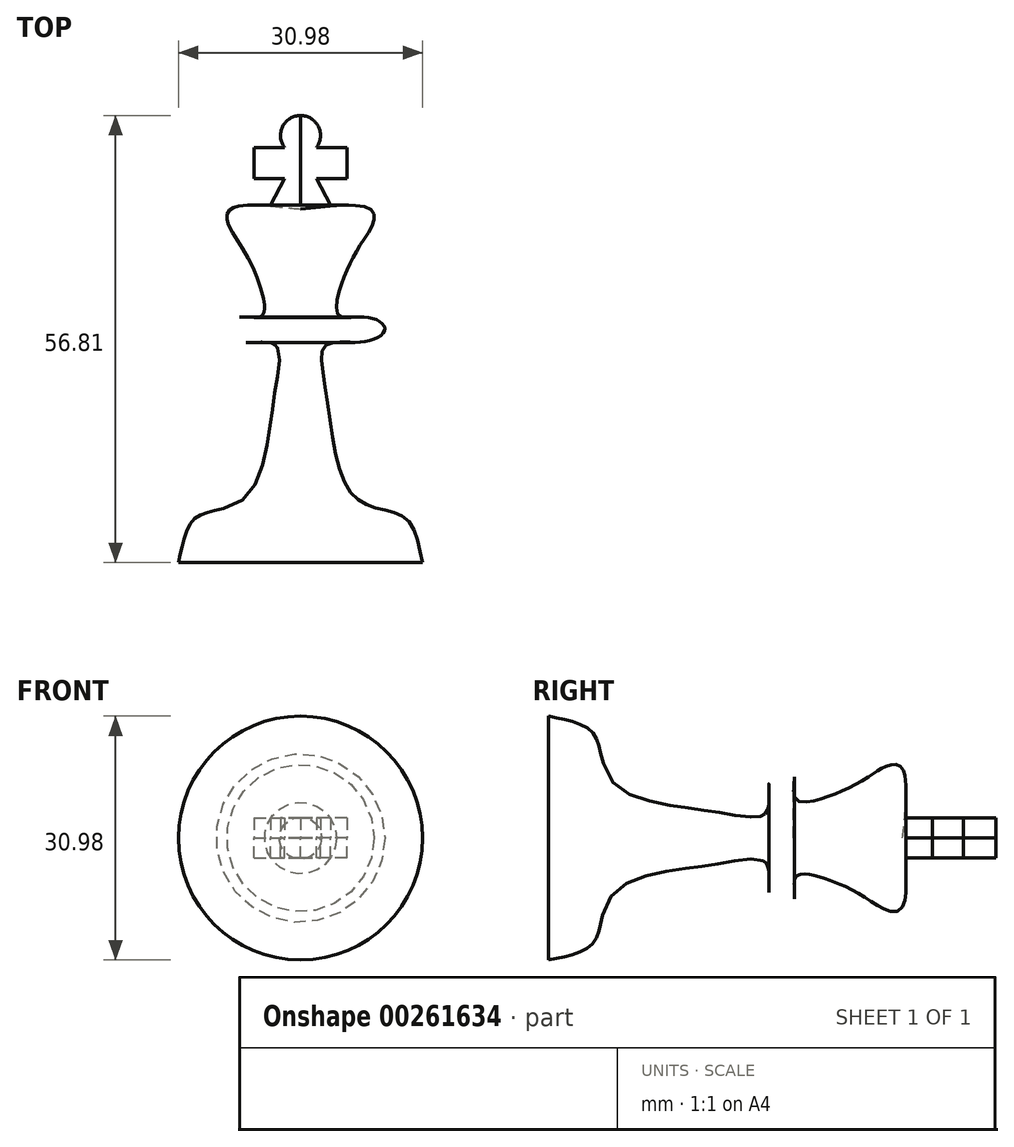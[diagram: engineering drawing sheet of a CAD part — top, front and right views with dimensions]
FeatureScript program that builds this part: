
annotation { "Feature Type Name" : "Feature", "Feature Type Description" : "" }
export const myFeature = defineFeature(function(context is Context, id is Id, definition is map)
    precondition{}
    {
        {
            var Q0;
            Q0=qCreatedBy(makeId("Top.planeOp"),FACE);
            var sketch = newSketch(context, id + "F0", { "sketchPlane" : qUnion([Q0])});
            skLineSegment(sketch, "E0", {"start": v(0, 0) * mm, "end": v(15.5, 0) * mm});
            skLineSegment(sketch, "E1", {"start": v(0, 0) * mm, "end": v(0, 44.92) * mm});
            skFitSpline(sketch, "E2", {"points": [v(0, 44.92) * mm, v(8.84, 44.92) * mm, v(9.25, 43.26) * mm, v(7.6, 40.35) * mm, v(6.14, 37.64) * mm, v(4.89, 34.32) * mm, v(4.89, 31.4) * mm, v(8.42, 31.2) * mm, v(10.71, 29.74) * mm, v(8.21, 28.08) * mm, v(3.22, 27.66) * mm, v(3.22, 21.84) * mm, v(5.93, 9.57) * mm, v(9.88, 6.86) * mm, v(13.62, 5.4) * mm, v(15.5, 0) * mm], "startDerivative": vector(118.77, 13.18) * mm, "endDerivative": vector(15.68, -75.67) * mm});
            skSolve(sketch);
        }
        {
            var Q0;
            Q0=makeQuery(id+"F0.imprint","IMPRINT",FACE,{"disambiguationData":[TD([[makeQuery(id+"F0.imprint","IMPRINT",EDGE,{"derivedFrom":sQuery(id+"F0.wireOp",EDGE,"E0")}),1.0]])]});
            var Q1;
            Q1=sQuery(id+"F0.wireOp",EDGE,"E1");
            revolve(context, id + "F1", {"entities" : qUnion([Q0]), "axis" : qUnion([Q1]), "revolveType" : RevolveType.FULL});
        }
        {
            var Q0;
            Q0=qCreatedBy(makeId("Top.planeOp"),FACE);
            var sketch = newSketch(context, id + "F2", { "sketchPlane" : qUnion([Q0])});
            skLineSegment(sketch, "E3", {"start": v(-3.81, 45.43) * mm, "end": v(-2.02, 48.8) * mm});
            skLineSegment(sketch, "E4", {"start": v(-2.02, 48.8) * mm, "end": v(-5.9, 48.8) * mm});
            skLineSegment(sketch, "E5", {"start": v(-5.9, 48.8) * mm, "end": v(-5.9, 52.73) * mm});
            skLineSegment(sketch, "E6", {"start": v(-5.9, 52.73) * mm, "end": v(-2.02, 52.73) * mm});
            skArc(sketch, "E7", {"start": v(0, 56.81) * mm, "mid": v(-2.28, 55.4) * mm, "end": v(-2.02, 52.73) * mm});
            skLineSegment(sketch, "E8", {"start": v(-3.8, 45.43) * mm, "end": v(0, 45.43) * mm});
            skLineSegment(sketch, "E9", {"start": v(0, 56.81) * mm, "end": v(0, 45.43) * mm});
            skSolve(sketch);
        }
        {
            var Q0;
            Q0 = qSketchRegion(id + "F2", true);
            extrude(context, id + "F3", {"entities" : qUnion([Q0]), "operationType" : NewBodyOperationType.ADD, "depth" : 2.54 * mm});
        }
        {
            var Q0;
            Q0=makeQuery(id+"F3.opExtrude","SWEPT_BODY",BODY,{"disambiguationData":[OSD([sQuery(id+"F2.wireOp",EDGE,"E3"),sQuery(id+"F2.wireOp",EDGE,"E4"),sQuery(id+"F2.wireOp",EDGE,"E5"),sQuery(id+"F2.wireOp",EDGE,"E6"),sQuery(id+"F2.wireOp",EDGE,"E7"),sQuery(id+"F2.wireOp",EDGE,"E8"),sQuery(id+"F2.wireOp",EDGE,"E9")])]});
            var Q1;
            Q1=qCreatedBy(makeId("Right.planeOp"),FACE);
            mirror(context, id + "F4", {"operationType" : NewBodyOperationType.ADD, "entities" : qUnion([Q0]), "mirrorPlane" : qUnion([Q1])});
        }
        {
            var Q0;
            Q0=makeQuery(id+"F4.opPattern","COPY",BODY,{"derivedFrom":makeQuery(id+"F3.opExtrude","SWEPT_BODY",BODY,{"disambiguationData":[OSD([sQuery(id+"F2.wireOp",EDGE,"E3"),sQuery(id+"F2.wireOp",EDGE,"E4"),sQuery(id+"F2.wireOp",EDGE,"E5"),sQuery(id+"F2.wireOp",EDGE,"E6"),sQuery(id+"F2.wireOp",EDGE,"E7"),sQuery(id+"F2.wireOp",EDGE,"E8"),sQuery(id+"F2.wireOp",EDGE,"E9")])]}),"instanceName":"1"});
            var Q1;
            Q1=makeQuery(id+"F3.opExtrude","SWEPT_BODY",BODY,{"disambiguationData":[OSD([sQuery(id+"F2.wireOp",EDGE,"E3"),sQuery(id+"F2.wireOp",EDGE,"E4"),sQuery(id+"F2.wireOp",EDGE,"E5"),sQuery(id+"F2.wireOp",EDGE,"E6"),sQuery(id+"F2.wireOp",EDGE,"E7"),sQuery(id+"F2.wireOp",EDGE,"E8"),sQuery(id+"F2.wireOp",EDGE,"E9")])]});
            var Q2;
            Q2=qCreatedBy(makeId("Top.planeOp"),FACE);
            mirror(context, id + "F5", {"operationType" : NewBodyOperationType.ADD, "entities" : qUnion([Q0, Q1]), "mirrorPlane" : qUnion([Q2])});
        }
    });
